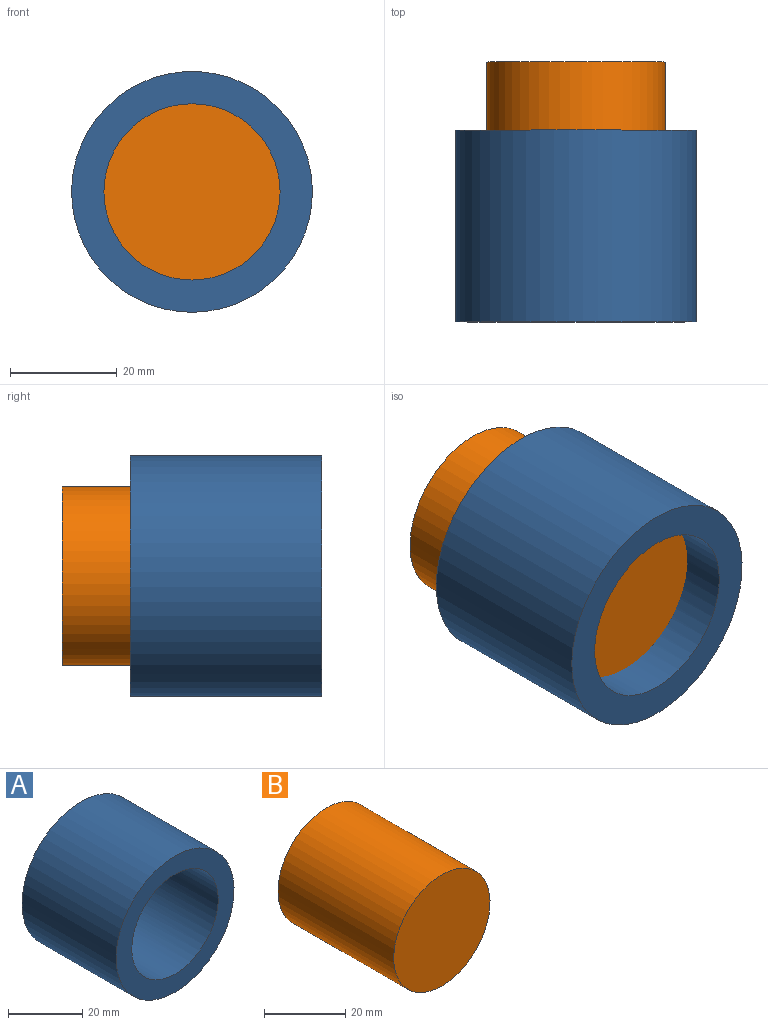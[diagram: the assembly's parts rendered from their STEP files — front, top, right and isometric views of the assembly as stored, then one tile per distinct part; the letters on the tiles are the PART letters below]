
ASSEMBLY  parts=2 mates=1
PART A: 4 faces, bbox 45.1x35.9x45.1 mm
  f0: cylinder r=22.54mm len=45.08mm, axis (0,1,0), area 5084.4mm2, adj f1,f2
  f1: plane 45.08x45.08mm, normal (0,-1,0), area 740.9mm2, adj f0,f3
  f2: plane 45.08x45.08mm, normal (0,1,0), area 740.9mm2, adj f0,f3
  f3: cylinder r=16.5mm len=35.9mm, axis (0,1,0), area 3721.8mm2, adj f1,f2
PART B: 3 faces, bbox 33.5x40.2x33.5 mm
  f0: cylinder r=16.73mm len=40.2mm, axis (0,1,0), area 4226.4mm2, adj f1,f2
  f1: plane 33.47x33.47mm, normal (0,-1,0), area 879.6mm2, adj f0
  f2: plane 33.47x33.47mm, normal (0,1,0), area 879.6mm2, adj f0
PLACE A rot(axis=(-0.53,-0.02,0.85),0deg) t=(28.18,-26.14,10.2)mm
PLACE B t=(28.18,-13.37,10.2)mm
MATE slider B.f0 <-> A.f3  axis (0,-1,0) through (28.18,-53.57,10.2)mm
